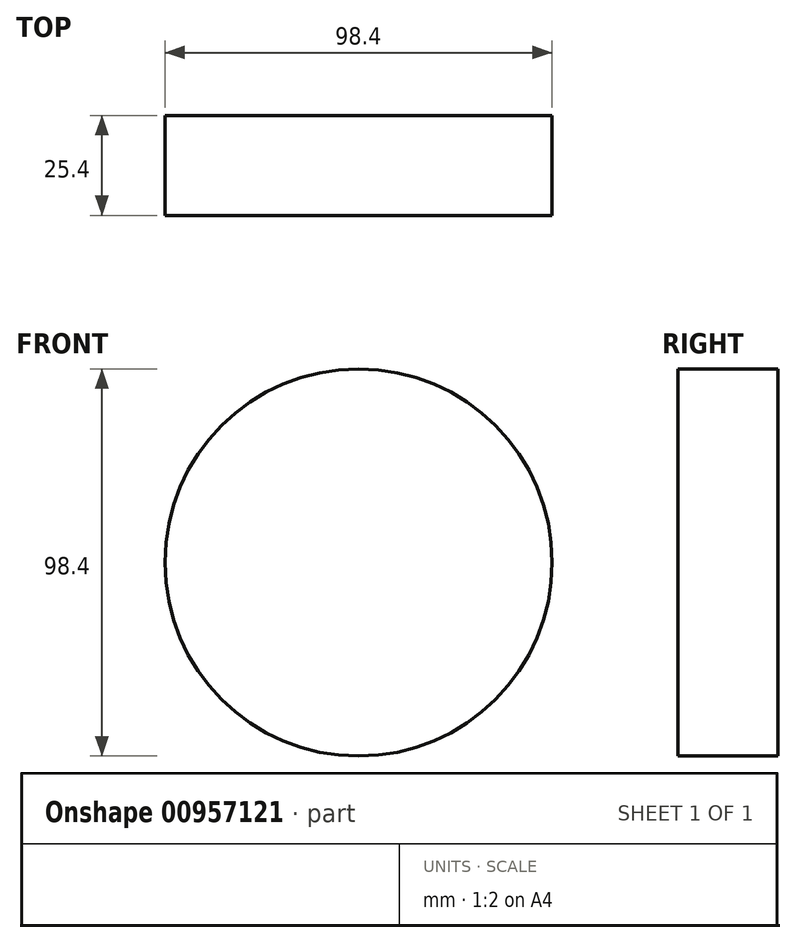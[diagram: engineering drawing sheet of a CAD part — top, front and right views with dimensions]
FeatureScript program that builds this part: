
annotation { "Feature Type Name" : "Feature", "Feature Type Description" : "" }
export const myFeature = defineFeature(function(context is Context, id is Id, definition is map)
    precondition{}
    {
        {
            var Q0;
            Q0=qCreatedBy(makeId("Front.planeOp"),FACE);
            var sketch = newSketch(context, id + "F0", { "sketchPlane" : qUnion([Q0])});
            skCircle(sketch, "E0", {"center": v(0, 0) * mm, "radius": 49.2 * mm});
            skSolve(sketch);
        }
        {
            var Q0;
            Q0=makeQuery(id+"F0.imprint","IMPRINT",FACE,{"disambiguationData":[TD([[makeQuery(id+"F0.imprint","IMPRINT",EDGE,{"derivedFrom":sQuery(id+"F0.wireOp",EDGE,"E0")}),1.0]])]});
            var Q1;
            Q1=sQuery(id+"F0.wireOp",EDGE,"E0");
            extrude(context, id + "F1", {"entities" : qUnion([Q0]), "surfaceEntities" : qUnion([Q1]), "depth" : 25.4 * mm, "offsetDistance" : 25.4 * mm});
        }
    });
